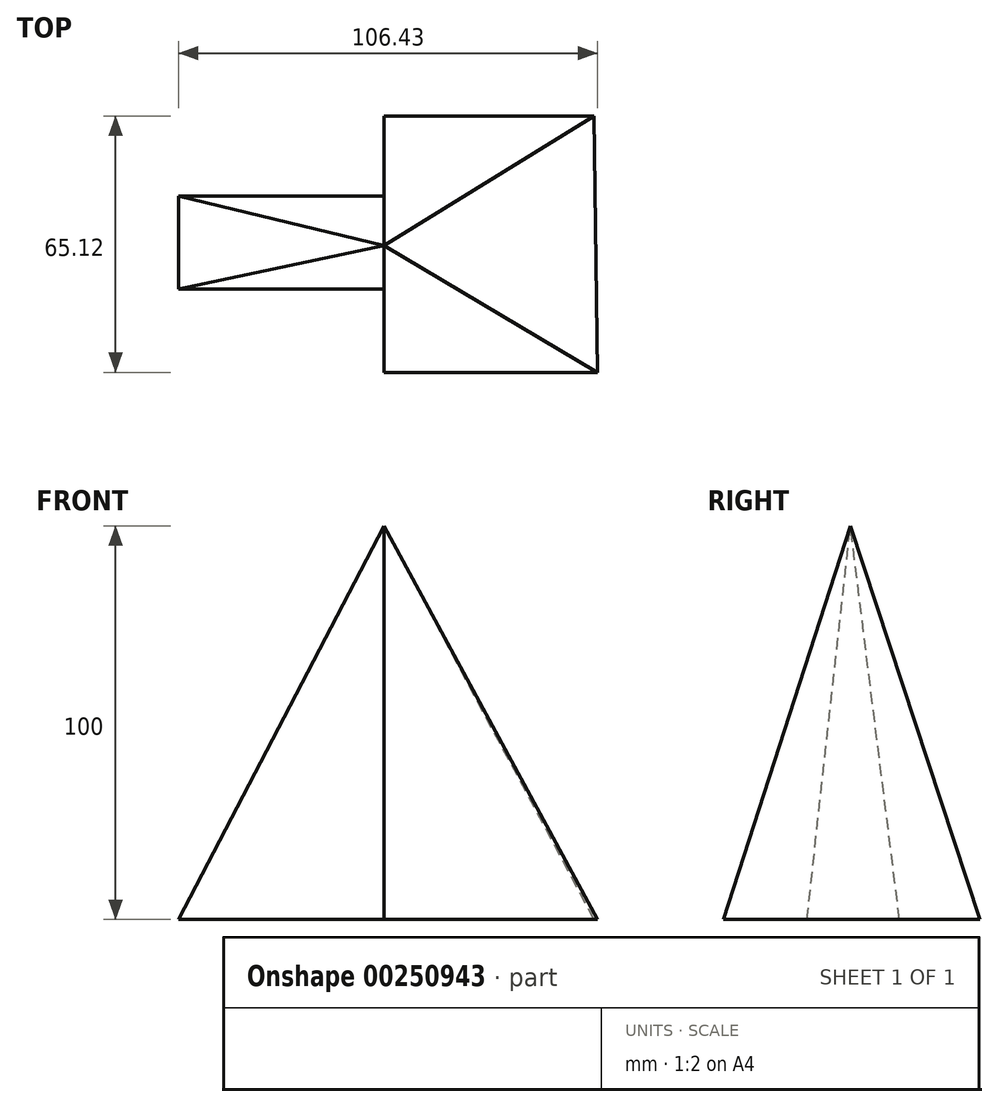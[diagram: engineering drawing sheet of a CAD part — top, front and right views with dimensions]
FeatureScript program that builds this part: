
annotation { "Feature Type Name" : "Feature", "Feature Type Description" : "" }
export const myFeature = defineFeature(function(context is Context, id is Id, definition is map)
    precondition{}
    {
        {
            var Q0;
            Q0=qCreatedBy(makeId("Top.planeOp"),FACE);
            var sketch = newSketch(context, id + "F0", { "sketchPlane" : qUnion([Q0])});
            skLineSegment(sketch, "E0", {"start": v(0, 32.85) * mm, "end": v(53.36, 32.85) * mm});
            skLineSegment(sketch, "E1", {"start": v(0, 32.85) * mm, "end": v(0, 12.48) * mm});
            skLineSegment(sketch, "E2", {"start": v(0, 12.48) * mm, "end": v(-52.21, 12.48) * mm});
            skLineSegment(sketch, "E3", {"start": v(-52.21, 12.48) * mm, "end": v(-52.21, -11.05) * mm});
            skLineSegment(sketch, "E4", {"start": v(-52.21, -11.05) * mm, "end": v(0, -11.05) * mm});
            skLineSegment(sketch, "E5", {"start": v(0, -11.05) * mm, "end": v(0, -32.27) * mm});
            skLineSegment(sketch, "E6", {"start": v(0, -32.27) * mm, "end": v(54.22, -32.27) * mm});
            skLineSegment(sketch, "E7", {"start": v(53.36, 32.85) * mm, "end": v(54.22, -32.27) * mm});
            skPoint(sketch, "E8", {"position": v(0, 0) * mm});
            skSolve(sketch);
        }
        {
            var Q0;
            Q0=qCreatedBy(makeId("Top.planeOp"),FACE);
            cPlane(context, id + "F1", {"entities" : qUnion([Q0]), "cplaneType" : CPlaneType.OFFSET, "offset" : 100 * mm, "width" : 150 * mm, "height" : 150 * mm});
        }
        {
            var Q0;
            Q0=qCreatedBy(id+"F1.planeOp",FACE);
            var sketch = newSketch(context, id + "F2", { "sketchPlane" : qUnion([Q0])});
            skPoint(sketch, "E9", {"position": v(0, 0) * mm});
            skSolve(sketch);
        }
        {
            var Q0;
            Q0=makeQuery(id+"F0.imprint","IMPRINT",FACE,{"disambiguationData":[TD([[makeQuery(id+"F0.imprint","IMPRINT",EDGE,{"derivedFrom":sQuery(id+"F0.wireOp",EDGE,"E0")}),-1.0]])]});
            var Q1;
            Q1=sQuery(id+"F2.wireOp",VERTEX,"E9");
            loft(context, id + "F3", {"sheetProfilesArray" : [{ "sheetProfileEntities" : qUnion([Q0]) }, { "sheetProfileEntities" : qUnion([Q1]) }]});
        }
    });
